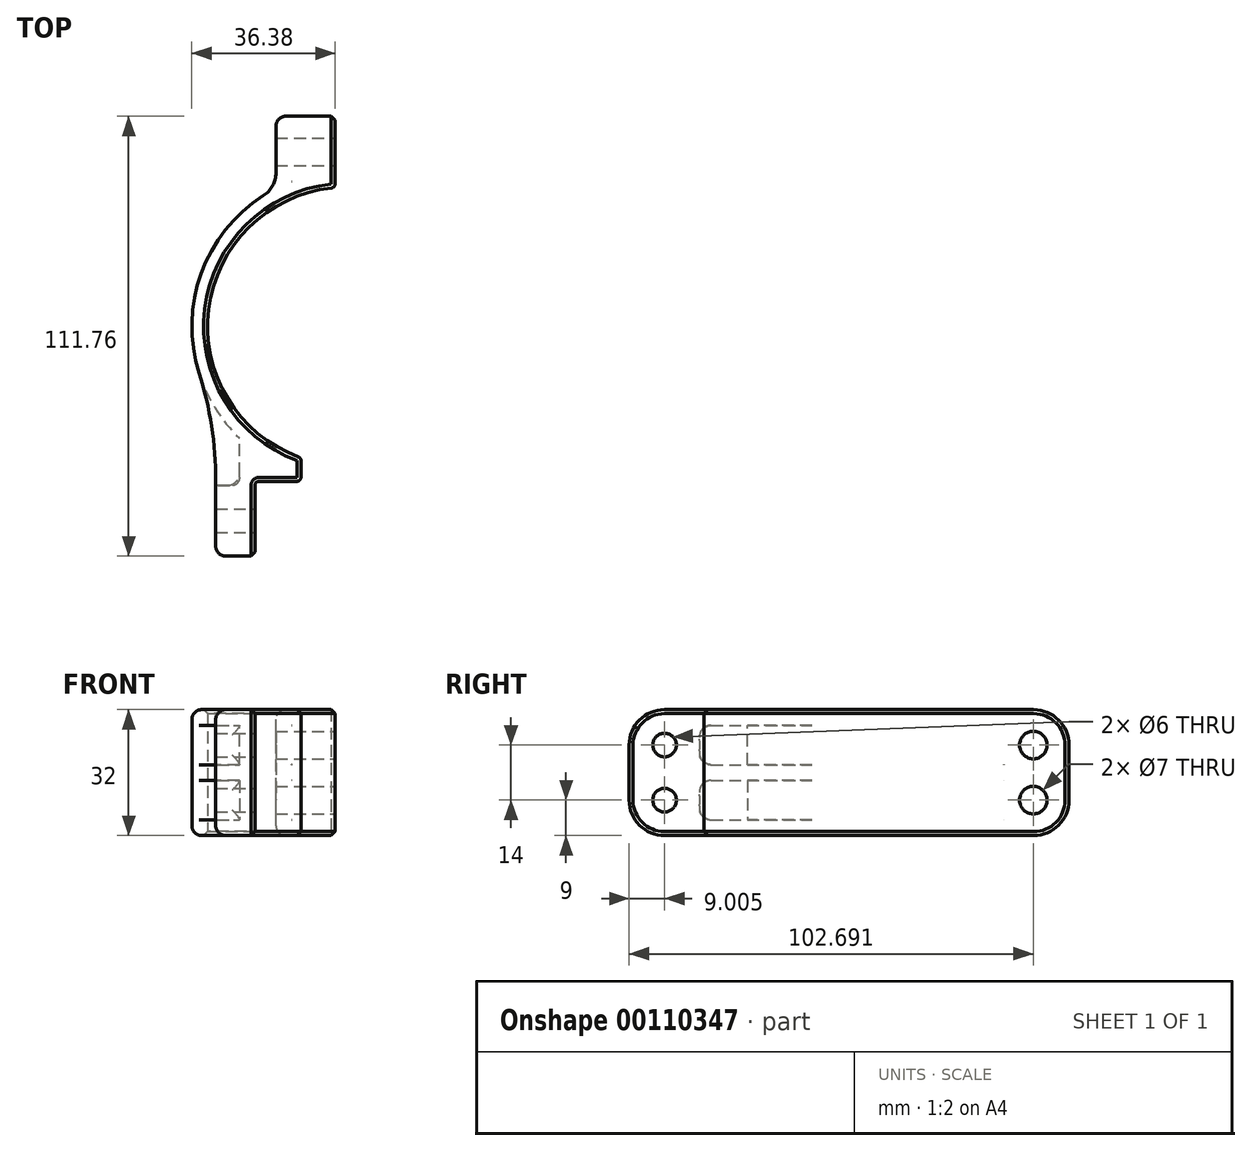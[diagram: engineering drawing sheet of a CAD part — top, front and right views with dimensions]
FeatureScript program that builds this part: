
annotation { "Feature Type Name" : "Feature", "Feature Type Description" : "" }
export const myFeature = defineFeature(function(context is Context, id is Id, definition is map)
    precondition{}
    {
        {
            var Q0;
            Q0=qCreatedBy(makeId("Top.planeOp"),FACE);
            var sketch = newSketch(context, id + "F0", { "sketchPlane" : qUnion([Q0])});
            skCircle(sketch, "E0", {"center": v(0, 0) * mm, "radius": 35.38 * mm, "construction": true});
            skLineSegment(sketch, "E1", {"start": v(0, 0) * mm, "end": v(0, 35.38) * mm, "construction": true});
            skLineSegment(sketch, "E2", {"start": v(0, 35.38) * mm, "end": v(0, 53.38) * mm, "construction": true});
            skLineSegment(sketch, "E3", {"start": v(3, 35.25) * mm, "end": v(3, 53.38) * mm, "construction": true});
            skLineSegment(sketch, "E4", {"start": v(3, 53.38) * mm, "end": v(18, 53.38) * mm, "construction": true});
            skLineSegment(sketch, "E5.MirrorCS", {"start": v(-3, 35.25) * mm, "end": v(-3, 53.38) * mm});
            skLineSegment(sketch, "E6.MirrorCS", {"start": v(-3, 53.38) * mm, "end": v(-18, 53.38) * mm});
            skCircle(sketch, "E7", {"center": v(0, 0) * mm, "radius": 39.38 * mm, "construction": true});
            skLineSegment(sketch, "E8", {"start": v(-18, 53.38) * mm, "end": v(-18, 35.02) * mm});
            skLineSegment(sketch, "E9.MirrorCS", {"start": v(18, 53.38) * mm, "end": v(18, 35.02) * mm, "construction": true});
            skLineSegment(sketch, "E10", {"start": v(0, -39.38) * mm, "end": v(0, -58.37) * mm, "construction": true});
            skLineSegment(sketch, "E11", {"start": v(-23.3, -26.62) * mm, "end": v(-23.3, -58.37) * mm, "construction": true});
            skLineSegment(sketch, "E12", {"start": v(0, -39.38) * mm, "end": v(-23.3, -39.38) * mm, "construction": true});
            skLineSegment(sketch, "E13", {"start": v(-11.65, -39.38) * mm, "end": v(-11.65, -33.4) * mm});
            skLineSegment(sketch, "E14", {"start": v(-11.65, -39.38) * mm, "end": v(-23.3, -39.38) * mm});
            skLineSegment(sketch, "E15", {"start": v(-33.3, -21.01) * mm, "end": v(-33.3, -58.37) * mm});
            skLineSegment(sketch, "E16", {"start": v(-33.3, -58.37) * mm, "end": v(-23.3, -58.37) * mm});
            skLineSegment(sketch, "E17", {"start": v(-23.3, -58.37) * mm, "end": v(-23.3, -39.38) * mm});
            skArc(sketch, "E18", {"start": v(-33.3, -21.01) * mm, "mid": v(-37.98, 10.37) * mm, "end": v(-18, 35.02) * mm});
            skArc(sketch, "E19", {"start": v(-3, 35.25) * mm, "mid": v(-35.1, 4.42) * mm, "end": v(-11.65, -33.4) * mm});
            skLineSegment(sketch, "E20.MirrorCS", {"start": v(11.65, -39.38) * mm, "end": v(11.65, -33.4) * mm, "construction": true});
            skLineSegment(sketch, "E21.MirrorCS", {"start": v(0, -39.37) * mm, "end": v(23.3, -39.37) * mm, "construction": true});
            skLineSegment(sketch, "E22.MirrorCS", {"start": v(23.3, -26.62) * mm, "end": v(23.3, -58.37) * mm, "construction": true});
            skLineSegment(sketch, "E23.MirrorCS", {"start": v(33.3, -58.37) * mm, "end": v(23.3, -58.37) * mm, "construction": true});
            skLineSegment(sketch, "E24.MirrorCS", {"start": v(33.3, -21.01) * mm, "end": v(33.3, -58.37) * mm, "construction": true});
            skSolve(sketch);
        }
        {
            var Q0;
            Q0=makeQuery(id+"F0.imprint","IMPRINT",FACE,{"disambiguationData":[TD([[makeQuery(id+"F0.imprint","IMPRINT",EDGE,{"derivedFrom":sQuery(id+"F0.wireOp",EDGE,"E5.MirrorCS")}),1.0]])]});
            extrude(context, id + "F1", {"entities" : qUnion([Q0]), "depth" : 18 * mm});
        }
        {
            var Q0;
            Q0=makeQuery(id+"F1.opExtrude","SWEPT_FACE",FACE,{"disambiguationData":[OSD([sQuery(id+"F0.wireOp",EDGE,"E5.MirrorCS")])]});
            var sketch = newSketch(context, id + "F2", { "sketchPlane" : qUnion([Q0])});
            skPoint(sketch, "E25", {"position": v(44.31, 9) * mm});
            skPoint(sketch, "E25.positionSnap0", {"position": v(44.31, 18) * mm});
            skPoint(sketch, "E25.positionSnap1", {"position": v(35.25, 9) * mm});
            skCircle(sketch, "E26", {"center": v(44.31, 9) * mm, "radius": 3.5 * mm});
            skSolve(sketch);
        }
        {
            var Q0;
            Q0=makeQuery(id+"F2.imprint","IMPRINT",FACE,{"disambiguationData":[TD([[makeQuery(id+"F2.imprint","IMPRINT",EDGE,{"derivedFrom":sQuery(id+"F2.wireOp",EDGE,"E26")}),1.0]])]});
            extrude(context, id + "F3", {"entities" : qUnion([Q0]), "operationType" : NewBodyOperationType.REMOVE, "oppositeDirection" : true, "depth" : 25 * mm});
        }
        {
            var Q0;
            Q0=makeQuery(id+"F1.opExtrude","SWEPT_FACE",FACE,{"disambiguationData":[OSD([sQuery(id+"F0.wireOp",EDGE,"E17")])]});
            var sketch = newSketch(context, id + "F4", { "sketchPlane" : qUnion([Q0])});
            skPoint(sketch, "E27", {"position": v(-49.37, 9) * mm});
            skPoint(sketch, "E27.positionSnap0", {"position": v(-39.37, 9) * mm});
            skCircle(sketch, "E28", {"center": v(-49.37, 9) * mm, "radius": 3 * mm});
            skSolve(sketch);
        }
        {
            var Q0;
            Q0=makeQuery(id+"F4.imprint","IMPRINT",FACE,{"disambiguationData":[TD([[makeQuery(id+"F4.imprint","IMPRINT",EDGE,{"derivedFrom":sQuery(id+"F4.wireOp",EDGE,"E28")}),1.0]])]});
            extrude(context, id + "F5", {"entities" : qUnion([Q0]), "operationType" : NewBodyOperationType.REMOVE, "endBound" : BoundingType.THROUGH_ALL, "oppositeDirection" : true, "depth" : 25 * mm});
        }
        {
            var Q0;
            Q0=makeQuery(id+"F1.opExtrude","CAP_EDGE",EDGE,{"disambiguationData":[OSD([sQuery(id+"F0.wireOp",EDGE,"E6.MirrorCS")])],"isStart":true});
            var Q1;
            Q1=makeQuery(id+"F1.opExtrude","CAP_EDGE",EDGE,{"disambiguationData":[OSD([sQuery(id+"F0.wireOp",EDGE,"E16")])],"isStart":true});
            fillet(context, id + "F6", {"entities" : qUnion([Q0, Q1]), "radius" : 9 * mm, "tangentPropagation" : true, "allowEdgeOverflow" : false});
        }
        {
            var Q0;
            Q0=makeQuery(id+"F1.opExtrude","SWEPT_FACE",FACE,{"disambiguationData":[OSD([sQuery(id+"F0.wireOp",EDGE,"E8")])]});
            var sketch = newSketch(context, id + "F7", { "sketchPlane" : qUnion([Q0])});
            skPoint(sketch, "E29", {"position": v(-44.31, 9) * mm});
            skCircle(sketch, "E30", {"center": v(-44.31, 9) * mm, "radius": 5 * mm});
            skSolve(sketch);
        }
        {
            var Q0;
            Q0=makeQuery(id+"F1.opExtrude","SWEPT_FACE",FACE,{"disambiguationData":[OSD([sQuery(id+"F0.wireOp",EDGE,"E15")])]});
            var sketch = newSketch(context, id + "F8", { "sketchPlane" : qUnion([Q0])});
            skPoint(sketch, "E31", {"position": v(49.38, 9) * mm});
            skCircle(sketch, "E32", {"center": v(49.38, 9) * mm, "radius": 5 * mm});
            skSolve(sketch);
        }
        {
            var Q0;
            Q0=makeQuery(id+"F7.imprint","IMPRINT",FACE,{"disambiguationData":[TD([[makeQuery(id+"F7.imprint","IMPRINT",EDGE,{"derivedFrom":sQuery(id+"F7.wireOp",EDGE,"E30")}),1.0]])]});
            extrude(context, id + "F9", {"entities" : qUnion([Q0]), "operationType" : NewBodyOperationType.REMOVE, "oppositeDirection" : true, "depth" : 6 * mm});
        }
        {
            var Q0;
            Q0=makeQuery(id+"F8.imprint","IMPRINT",FACE,{"disambiguationData":[TD([[makeQuery(id+"F8.imprint","IMPRINT",EDGE,{"derivedFrom":sQuery(id+"F8.wireOp",EDGE,"E32")}),1.0]])]});
            extrude(context, id + "F10", {"entities" : qUnion([Q0]), "operationType" : NewBodyOperationType.REMOVE, "oppositeDirection" : true, "depth" : 4 * mm});
        }
        {
            var Q0;
            Q0=makeQuery(id+"F1.opExtrude","SWEPT_FACE",FACE,{"disambiguationData":[OSD([sQuery(id+"F0.wireOp",EDGE,"E15")])]});
            shell(context, id + "F11", {"entities" : qUnion([Q0]), "thickness" : 4 * mm});
        }
        {
            var Q0;
            Q0=makeQuery(id+"F11.opShell","OFFSET_FACE",FACE,{"disambiguationData":[OSD([sQuery(id+"F0.wireOp",EDGE,"E14")])]});
            var Q1;
            Q1=makeQuery(id+"F11.opShell","OFFSET_FACE",FACE,{"disambiguationData":[OSD([sQuery(id+"F0.wireOp",EDGE,"E19")]),OD(0.0)]});
            extrude(context, id + "F12", {"entities" : qUnion([Q0]), "operationType" : NewBodyOperationType.ADD, "endBound" : BoundingType.UP_TO_SURFACE, "endBoundEntityFace" : qUnion([Q1]), "depth" : 25 * mm});
        }
        {
            var Q0;
            Q0=makeQuery(id+"F1.opExtrude","SWEPT_EDGE",EDGE,{"disambiguationData":[OSD([sQuery(id+"F0.wireOp",EDGE,"E8"),sQuery(id+"F0.wireOp",EDGE,"E18")])]});
            var Q1;
            Q1=makeQuery(id+"F12.opExtrude","CAP_EDGE",EDGE,{"disambiguationData":[OSD([sQuery(id+"F0.wireOp",EDGE,"E14"),sQuery(id+"F0.wireOp",EDGE,"E17")])],"isStart":false});
            fillet(context, id + "F13", {"entities" : qUnion([Q0, Q1]), "radius" : 7 * mm, "tangentPropagation" : true, "allowEdgeOverflow" : false});
        }
        {
            var Q0;
            Q0=makeQuery(id+"F11.opShell","OFFSET_EDGE",EDGE,{"disambiguationData":[OSD([sQuery(id+"F0.wireOp",EDGE,"E15"),sQuery(id+"F0.wireOp",EDGE,"E18")])]});
            var Q1;
            Q1=makeQuery(id+"F1.opExtrude","SWEPT_EDGE",EDGE,{"disambiguationData":[OSD([sQuery(id+"F0.wireOp",EDGE,"E15"),sQuery(id+"F0.wireOp",EDGE,"E18")])]});
            fillet(context, id + "F14", {"entities" : qUnion([Q0, Q1]), "radius" : 90 * mm, "tangentPropagation" : true, "allowEdgeOverflow" : false});
        }
        {
            var Q0;
            Q0=makeQuery(id+"F11.opShell","TWEAK_EDGE",EDGE,{"derivedFrom":[makeQuery(id+"F1.opExtrude","CAP_FACE",FACE,{"disambiguationData":[OSD([sQuery(id+"F0.wireOp",EDGE,"E5.MirrorCS"),sQuery(id+"F0.wireOp",EDGE,"E6.MirrorCS"),sQuery(id+"F0.wireOp",EDGE,"E8"),sQuery(id+"F0.wireOp",EDGE,"E13"),sQuery(id+"F0.wireOp",EDGE,"E14"),sQuery(id+"F0.wireOp",EDGE,"E15"),sQuery(id+"F0.wireOp",EDGE,"E16"),sQuery(id+"F0.wireOp",EDGE,"E17"),sQuery(id+"F0.wireOp",EDGE,"E18"),sQuery(id+"F0.wireOp",EDGE,"E19")])],"isStart":true}),makeQuery(id+"F10.boolean.opBoolean","COPY",FACE,{"derivedFrom":makeQuery(id+"F10.opExtrude","SWEPT_FACE",FACE,{"disambiguationData":[OSD([sQuery(id+"F8.wireOp",EDGE,"E32")])]})})]});
            var Q1;
            Q1=makeQuery(id+"F11.opShell","TWEAK_EDGE",EDGE,{"derivedFrom":[makeQuery(id+"F1.opExtrude","CAP_FACE",FACE,{"disambiguationData":[OSD([sQuery(id+"F0.wireOp",EDGE,"E5.MirrorCS"),sQuery(id+"F0.wireOp",EDGE,"E6.MirrorCS"),sQuery(id+"F0.wireOp",EDGE,"E8"),sQuery(id+"F0.wireOp",EDGE,"E13"),sQuery(id+"F0.wireOp",EDGE,"E14"),sQuery(id+"F0.wireOp",EDGE,"E15"),sQuery(id+"F0.wireOp",EDGE,"E16"),sQuery(id+"F0.wireOp",EDGE,"E17"),sQuery(id+"F0.wireOp",EDGE,"E18"),sQuery(id+"F0.wireOp",EDGE,"E19")])],"isStart":false}),makeQuery(id+"F10.boolean.opBoolean","COPY",FACE,{"derivedFrom":makeQuery(id+"F10.opExtrude","SWEPT_FACE",FACE,{"disambiguationData":[OSD([sQuery(id+"F8.wireOp",EDGE,"E32")])]})})]});
            var Q2;
            {var subQ0=sQuery(id+"F0.wireOp",EDGE,"E17");var subQ1=sQuery(id+"F0.wireOp",EDGE,"E14");Q2=makeQuery(id+"F12.boolean.opBoolean","MERGE",EDGE,{"derivedFrom":[makeQuery(id+"F11.opShell","OFFSET_EDGE",EDGE,{"disambiguationData":[OSD([subQ0]),TDD([makeQuery(id+"F1.opExtrude","CAP_EDGE",EDGE,{"disambiguationData":[OSD([subQ0])],"isStart":true})])]}),makeQuery(id+"F12.opExtrude","SWEPT_EDGE",EDGE,{"disambiguationData":[OSD([subQ1,subQ0]),TDD([makeQuery(id+"F11.opShell","OFFSET_VERTEX",VERTEX,{"disambiguationData":[OSD([subQ1,subQ0]),TDD([makeQuery(id+"F1.opExtrude","CAP_VERTEX",VERTEX,{"disambiguationData":[OSD([subQ1,subQ0])],"isStart":true})])]})])]})]});}
            var Q3;
            {var subQ0=sQuery(id+"F0.wireOp",EDGE,"E17");var subQ1=sQuery(id+"F0.wireOp",EDGE,"E14");Q3=makeQuery(id+"F12.boolean.opBoolean","MERGE",EDGE,{"derivedFrom":[makeQuery(id+"F11.opShell","OFFSET_EDGE",EDGE,{"disambiguationData":[OSD([subQ0]),TDD([makeQuery(id+"F1.opExtrude","CAP_EDGE",EDGE,{"disambiguationData":[OSD([subQ0])],"isStart":false})])]}),makeQuery(id+"F12.opExtrude","SWEPT_EDGE",EDGE,{"disambiguationData":[OSD([subQ1,subQ0]),TDD([makeQuery(id+"F11.opShell","OFFSET_VERTEX",VERTEX,{"disambiguationData":[OSD([subQ1,subQ0]),TDD([makeQuery(id+"F1.opExtrude","CAP_VERTEX",VERTEX,{"disambiguationData":[OSD([subQ1,subQ0])],"isStart":false})])]})])]})]});}
            var Q4;
            Q4=makeQuery(id+"F11.opShell","TWEAK_EDGE",EDGE,{"derivedFrom":[makeQuery(id+"F1.opExtrude","SWEPT_FACE",FACE,{"disambiguationData":[OSD([sQuery(id+"F0.wireOp",EDGE,"E17")])]}),makeQuery(id+"F10.boolean.opBoolean","COPY",FACE,{"derivedFrom":makeQuery(id+"F10.opExtrude","SWEPT_FACE",FACE,{"disambiguationData":[OSD([sQuery(id+"F8.wireOp",EDGE,"E32")])]})})]});
            fillet(context, id + "F15", {"entities" : qUnion([Q0, Q1, Q2, Q3, Q4]), "radius" : 3 * mm, "tangentPropagation" : true, "allowEdgeOverflow" : false});
        }
        {
            var Q0;
            Q0=makeQuery(id+"F1.opExtrude","SWEPT_EDGE",EDGE,{"disambiguationData":[OSD([sQuery(id+"F0.wireOp",EDGE,"E5.MirrorCS"),sQuery(id+"F0.wireOp",EDGE,"E19")])]});
            var Q1;
            Q1=makeQuery(id+"F1.opExtrude","SWEPT_EDGE",EDGE,{"disambiguationData":[OSD([sQuery(id+"F0.wireOp",EDGE,"E13"),sQuery(id+"F0.wireOp",EDGE,"E19")])]});
            var Q2;
            Q2=makeQuery(id+"F1.opExtrude","SWEPT_EDGE",EDGE,{"disambiguationData":[OSD([sQuery(id+"F0.wireOp",EDGE,"E14"),sQuery(id+"F0.wireOp",EDGE,"E17")])]});
            var Q3;
            Q3=makeQuery(id+"F1.opExtrude","SWEPT_EDGE",EDGE,{"disambiguationData":[OSD([sQuery(id+"F0.wireOp",EDGE,"E13"),sQuery(id+"F0.wireOp",EDGE,"E14")])]});
            fillet(context, id + "F16", {"entities" : qUnion([Q0, Q1, Q2, Q3]), "radius" : 1 * mm, "tangentPropagation" : true, "allowEdgeOverflow" : false});
        }
        {
            var Q0;
            Q0=makeQuery(id+"F1.opExtrude","CAP_FACE",FACE,{"disambiguationData":[OSD([sQuery(id+"F0.wireOp",EDGE,"E5.MirrorCS"),sQuery(id+"F0.wireOp",EDGE,"E6.MirrorCS"),sQuery(id+"F0.wireOp",EDGE,"E8"),sQuery(id+"F0.wireOp",EDGE,"E13"),sQuery(id+"F0.wireOp",EDGE,"E14"),sQuery(id+"F0.wireOp",EDGE,"E15"),sQuery(id+"F0.wireOp",EDGE,"E16"),sQuery(id+"F0.wireOp",EDGE,"E17"),sQuery(id+"F0.wireOp",EDGE,"E18"),sQuery(id+"F0.wireOp",EDGE,"E19")])],"isStart":false});
            extrude(context, id + "F17", {"entities" : qUnion([Q0]), "operationType" : NewBodyOperationType.REMOVE, "oppositeDirection" : true, "depth" : 2 * mm});
        }
        {
            var Q0;
            Q0=makeQuery(id+"F1.opExtrude","SWEPT_BODY",BODY,{"disambiguationData":[OSD([sQuery(id+"F0.wireOp",EDGE,"E5.MirrorCS"),sQuery(id+"F0.wireOp",EDGE,"E6.MirrorCS"),sQuery(id+"F0.wireOp",EDGE,"E8"),sQuery(id+"F0.wireOp",EDGE,"E13"),sQuery(id+"F0.wireOp",EDGE,"E14"),sQuery(id+"F0.wireOp",EDGE,"E15"),sQuery(id+"F0.wireOp",EDGE,"E16"),sQuery(id+"F0.wireOp",EDGE,"E17"),sQuery(id+"F0.wireOp",EDGE,"E18"),sQuery(id+"F0.wireOp",EDGE,"E19")])]});
            var Q1;
            Q1=makeQuery(id+"F17.boolean.opBoolean","COPY",FACE,{"derivedFrom":makeQuery(id+"F17.opExtrude","CAP_FACE",FACE,{"disambiguationData":[OSD([sQuery(id+"F0.wireOp",EDGE,"E5.MirrorCS"),sQuery(id+"F0.wireOp",EDGE,"E6.MirrorCS"),sQuery(id+"F0.wireOp",EDGE,"E8"),sQuery(id+"F0.wireOp",EDGE,"E13"),sQuery(id+"F0.wireOp",EDGE,"E14"),sQuery(id+"F0.wireOp",EDGE,"E15"),sQuery(id+"F0.wireOp",EDGE,"E16"),sQuery(id+"F0.wireOp",EDGE,"E17"),sQuery(id+"F0.wireOp",EDGE,"E18"),sQuery(id+"F0.wireOp",EDGE,"E19")])],"isStart":false})});
            mirror(context, id + "F18", {"operationType" : NewBodyOperationType.ADD, "entities" : qUnion([Q0]), "mirrorPlane" : qUnion([Q1])});
        }
        {
            var Q0;
            Q0=makeQuery(id+"F18.opPattern","COPY",EDGE,{"derivedFrom":makeQuery(id+"F6.opFillet","BLEND_EDGE",EDGE,{"blendedFrom":[makeQuery(id+"F1.opExtrude","CAP_EDGE",EDGE,{"disambiguationData":[OSD([sQuery(id+"F0.wireOp",EDGE,"E16")])],"isStart":true}),makeQuery(id+"F1.opExtrude","SWEPT_FACE",FACE,{"disambiguationData":[OSD([sQuery(id+"F0.wireOp",EDGE,"E15")])]})],"blendedInto":[makeQuery(id+"F1.opExtrude","SWEPT_FACE",FACE,{"disambiguationData":[OSD([sQuery(id+"F0.wireOp",EDGE,"E15")])]})]}),"instanceName":"1"});
            fillet(context, id + "F19", {"entities" : qUnion([Q0]), "radius" : 2.5 * mm, "tangentPropagation" : true, "allowEdgeOverflow" : false});
        }
        {
            var Q0;
            Q0=makeQuery(id+"F1.opExtrude","CAP_EDGE",EDGE,{"disambiguationData":[OSD([sQuery(id+"F0.wireOp",EDGE,"E19")])],"isStart":true});
            var Q1;
            Q1=makeQuery(id+"F18.opPattern","COPY",EDGE,{"derivedFrom":makeQuery(id+"F1.opExtrude","CAP_EDGE",EDGE,{"disambiguationData":[OSD([sQuery(id+"F0.wireOp",EDGE,"E19")])],"isStart":true}),"instanceName":"1"});
            chamfer(context, id + "F20", {"entities" : qUnion([Q0, Q1]), "width" : 1 * mm, "tangentPropagation" : true});
        }
        {
            var Q0;
            Q0=makeQuery(id+"F18.opPattern","COPY",FACE,{"derivedFrom":makeQuery(id+"F10.boolean.opBoolean","COPY",FACE,{"derivedFrom":makeQuery(id+"F10.opExtrude","CAP_FACE",FACE,{"disambiguationData":[OSD([sQuery(id+"F0.wireOp",EDGE,"E15"),sQuery(id+"F4.wireOp",EDGE,"E28"),sQuery(id+"F8.wireOp",EDGE,"E32")])],"isStart":false})}),"instanceName":"1"});
            var Q1;
            Q1=makeQuery(id+"F10.boolean.opBoolean","COPY",FACE,{"derivedFrom":makeQuery(id+"F10.opExtrude","CAP_FACE",FACE,{"disambiguationData":[OSD([sQuery(id+"F0.wireOp",EDGE,"E15"),sQuery(id+"F4.wireOp",EDGE,"E28"),sQuery(id+"F8.wireOp",EDGE,"E32")])],"isStart":false})});
            extrude(context, id + "F21", {"entities" : qUnion([Q0, Q1]), "operationType" : NewBodyOperationType.ADD, "depth" : 4 * mm});
        }
        {
            var Q0;
            Q0=makeQuery(id+"F18.opPattern","COPY",FACE,{"derivedFrom":makeQuery(id+"F9.boolean.opBoolean","COPY",FACE,{"derivedFrom":makeQuery(id+"F9.opExtrude","CAP_FACE",FACE,{"disambiguationData":[OSD([sQuery(id+"F0.wireOp",EDGE,"E8"),sQuery(id+"F2.wireOp",EDGE,"E26"),sQuery(id+"F7.wireOp",EDGE,"E30")])],"isStart":false})}),"instanceName":"1"});
            var Q1;
            Q1=makeQuery(id+"F9.boolean.opBoolean","COPY",FACE,{"derivedFrom":makeQuery(id+"F9.opExtrude","CAP_FACE",FACE,{"disambiguationData":[OSD([sQuery(id+"F0.wireOp",EDGE,"E8"),sQuery(id+"F2.wireOp",EDGE,"E26"),sQuery(id+"F7.wireOp",EDGE,"E30")])],"isStart":false})});
            extrude(context, id + "F22", {"entities" : qUnion([Q0, Q1]), "operationType" : NewBodyOperationType.ADD, "depth" : 6 * mm});
        }
    });
